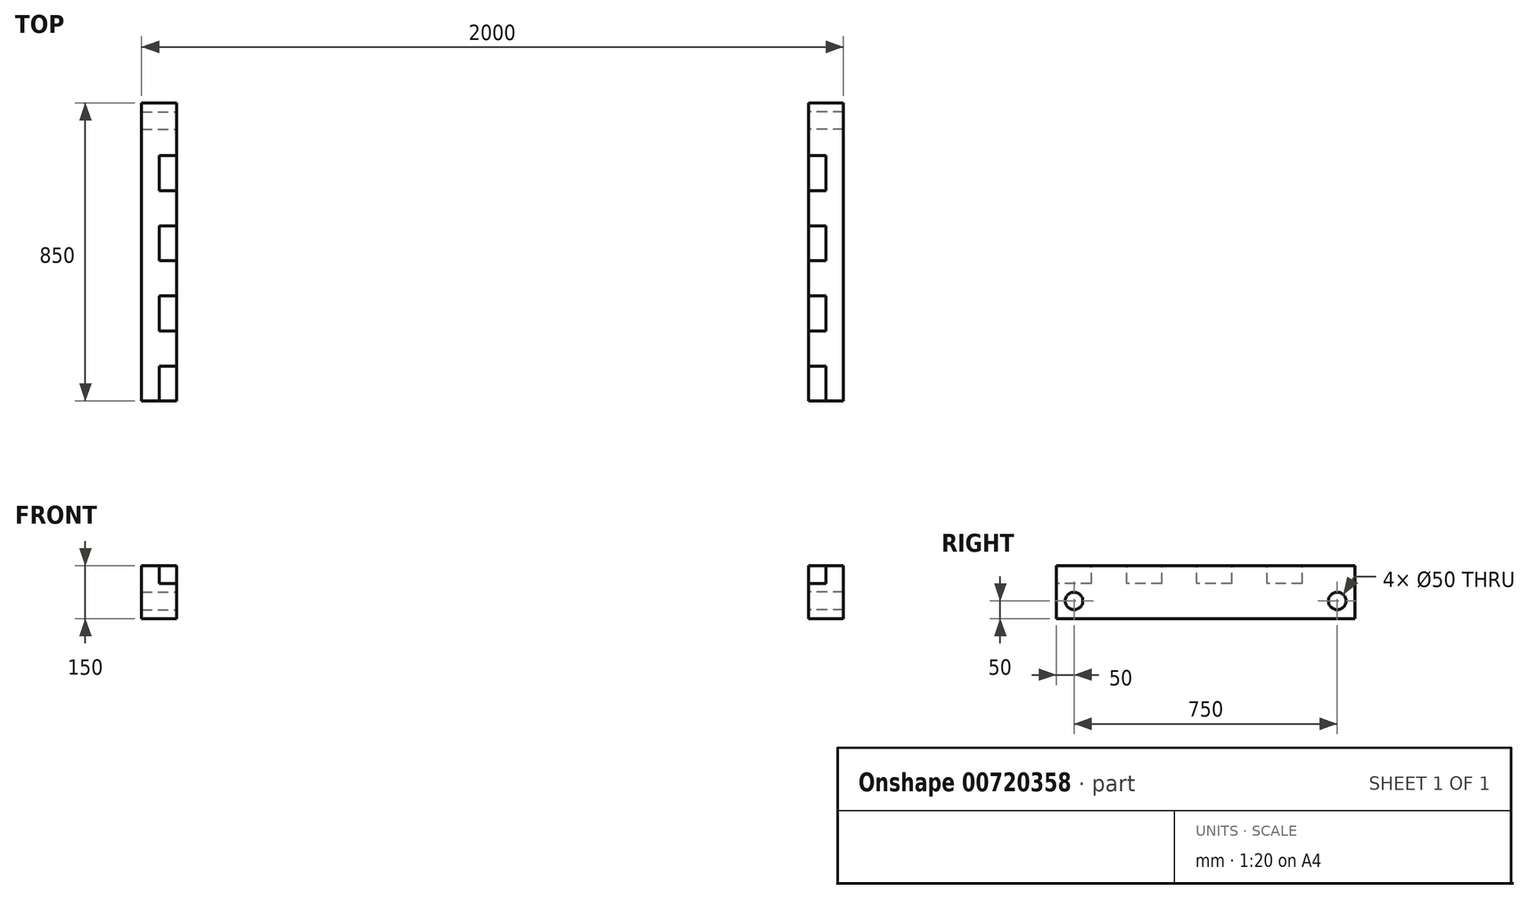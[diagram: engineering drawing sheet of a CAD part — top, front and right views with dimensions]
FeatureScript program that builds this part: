
annotation { "Feature Type Name" : "Feature", "Feature Type Description" : "" }
export const myFeature = defineFeature(function(context is Context, id is Id, definition is map)
    precondition{}
    {
        {
            var Q0;
            Q0=qCreatedBy(makeId("Top.planeOp"),FACE);
            var sketch = newSketch(context, id + "F0", { "sketchPlane" : qUnion([Q0])});
            skLineSegment(sketch, "E0.bottom", {"start": v(1000, 425) * mm, "end": v(-1000, 425) * mm});
            skLineSegment(sketch, "E0.top", {"start": v(1000, -425) * mm, "end": v(-1000, -425) * mm});
            skLineSegment(sketch, "E0.left", {"start": v(1000, 425) * mm, "end": v(1000, -425) * mm});
            skLineSegment(sketch, "E0.right", {"start": v(-1000, 425) * mm, "end": v(-1000, -425) * mm});
            skPoint(sketch, "E0.middle", {"position": v(0, 0) * mm});
            skSolve(sketch);
        }
        {
            var Q0;
            Q0=makeQuery(id+"F0.imprint","IMPRINT",FACE,{"disambiguationData":[TD([[makeQuery(id+"F0.imprint","IMPRINT",EDGE,{"derivedFrom":sQuery(id+"F0.wireOp",EDGE,"E0.bottom")}),1.0]])]});
            extrude(context, id + "F1", {"entities" : qUnion([Q0]), "depth" : 100 * mm, "offsetDistance" : 25 * mm});
        }
        {
            var Q0;
            Q0=makeQuery(id+"F1.opExtrude","CAP_FACE",FACE,{"disambiguationData":[OSD([sQuery(id+"F0.wireOp",EDGE,"E0.bottom"),sQuery(id+"F0.wireOp",EDGE,"E0.top"),sQuery(id+"F0.wireOp",EDGE,"E0.left"),sQuery(id+"F0.wireOp",EDGE,"E0.right")])],"isStart":true});
            var sketch = newSketch(context, id + "F2", { "sketchPlane" : qUnion([Q0])});
            skLineSegment(sketch, "E1.bottom", {"start": v(-900, 425) * mm, "end": v(900, 425) * mm});
            skLineSegment(sketch, "E1.top", {"start": v(-900, -425) * mm, "end": v(900, -425) * mm});
            skLineSegment(sketch, "E1.left", {"start": v(-900, 425) * mm, "end": v(-900, -425) * mm});
            skLineSegment(sketch, "E1.right", {"start": v(900, 425) * mm, "end": v(900, -425) * mm});
            skSolve(sketch);
        }
        {
            var Q0;
            {var subQ0=sQuery(id+"F2.wireOp",EDGE,"E1.left");Q0=makeQuery(id+"F2.imprint","IMPRINT",FACE,{"disambiguationData":[TD([[makeQuery(id+"F2.imprint","IMPRINT",EDGE,{"derivedFrom":subQ0}),-1.0]])]});}
            var Q1;
            {var subQ0=sQuery(id+"F2.wireOp",EDGE,"E1.right");Q1=makeQuery(id+"F2.imprint","IMPRINT",FACE,{"disambiguationData":[TD([[makeQuery(id+"F2.imprint","IMPRINT",EDGE,{"derivedFrom":subQ0}),1.0]])]});}
            extrude(context, id + "F3", {"entities" : qUnion([Q0, Q1]), "operationType" : NewBodyOperationType.ADD, "depth" : 100 * mm, "offsetDistance" : 25 * mm});
        }
        {
            var Q0;
            Q0=makeQuery(id+"F1.opExtrude","CAP_FACE",FACE,{"disambiguationData":[OSD([sQuery(id+"F0.wireOp",EDGE,"E0.bottom"),sQuery(id+"F0.wireOp",EDGE,"E0.top"),sQuery(id+"F0.wireOp",EDGE,"E0.left"),sQuery(id+"F0.wireOp",EDGE,"E0.right")])],"isStart":false});
            var sketch = newSketch(context, id + "F4", { "sketchPlane" : qUnion([Q0])});
            skLineSegment(sketch, "E2.bottom", {"start": v(-800, 425) * mm, "end": v(800, 425) * mm});
            skLineSegment(sketch, "E2.top", {"start": v(-800, -425) * mm, "end": v(800, -425) * mm});
            skLineSegment(sketch, "E2.left", {"start": v(-800, 425) * mm, "end": v(-800, -425) * mm});
            skLineSegment(sketch, "E2.right", {"start": v(800, 425) * mm, "end": v(800, -425) * mm});
            skSolve(sketch);
        }
        {
            var Q0;
            Q0 = qSketchRegion(id + "F4", true);
            extrude(context, id + "F5", {"entities" : qUnion([Q0]), "operationType" : NewBodyOperationType.REMOVE, "oppositeDirection" : true, "depth" : 120 * mm, "offsetDistance" : 25 * mm});
        }
        {
            var Q0;
            Q0=makeQuery(id+"F3.opExtrude","SWEPT_FACE",FACE,{"disambiguationData":[OSD([sQuery(id+"F2.wireOp",EDGE,"E1.left")])]});
            var sketch = newSketch(context, id + "F6", { "sketchPlane" : qUnion([Q0])});
            skCircle(sketch, "E3", {"center": v(-375, -50) * mm, "radius": 25 * mm});
            skPoint(sketch, "E3.centerSnap0", {"position": v(-425, -50) * mm});
            skCircle(sketch, "E4", {"center": v(375, -50) * mm, "radius": 25 * mm});
            skPoint(sketch, "E4.centerSnap0", {"position": v(425, -50) * mm});
            skSolve(sketch);
        }
        {
            var Q0;
            Q0 = qSketchRegion(id + "F6", true);
            extrude(context, id + "F7", {"entities" : qUnion([Q0]), "operationType" : NewBodyOperationType.REMOVE, "oppositeDirection" : true, "depth" : 150 * mm, "offsetDistance" : 25 * mm});
        }
        {
            var Q0;
            Q0=makeQuery(id+"F3.opExtrude","SWEPT_FACE",FACE,{"disambiguationData":[OSD([sQuery(id+"F2.wireOp",EDGE,"E1.right")])]});
            var sketch = newSketch(context, id + "F8", { "sketchPlane" : qUnion([Q0])});
            skCircle(sketch, "E5", {"center": v(375, -50) * mm, "radius": 25 * mm});
            skPoint(sketch, "E5.centerSnap0", {"position": v(425, -50) * mm});
            skCircle(sketch, "E6", {"center": v(-375, -50) * mm, "radius": 25 * mm});
            skPoint(sketch, "E6.centerSnap0", {"position": v(-425, -50) * mm});
            skSolve(sketch);
        }
        {
            var Q0;
            Q0 = qSketchRegion(id + "F8", true);
            extrude(context, id + "F9", {"entities" : qUnion([Q0]), "operationType" : NewBodyOperationType.REMOVE, "oppositeDirection" : true, "depth" : 100 * mm, "offsetDistance" : 25 * mm});
        }
        {
            var Q0;
            {var subQ0=sQuery(id+"F0.wireOp",EDGE,"E0.top");var subQ1=sQuery(id+"F0.wireOp",EDGE,"E0.right");var subQ2=sQuery(id+"F0.wireOp",EDGE,"E0.bottom");var subQ3=sQuery(id+"F0.wireOp",EDGE,"E0.left");Q0=makeQuery(id+"F5.boolean.opBoolean","SPLIT",FACE,{"disambiguationData":[TD([makeQuery(id+"F1.opExtrude","SWEPT_FACE",FACE,{"disambiguationData":[OSD([subQ1])]})])],"derivedFrom":makeQuery(id+"F1.opExtrude","CAP_FACE",FACE,{"disambiguationData":[OSD([subQ2,subQ0,subQ3,subQ1])],"isStart":false})});}
            extrude(context, id + "F10", {"entities" : qUnion([Q0]), "operationType" : NewBodyOperationType.REMOVE, "oppositeDirection" : true, "depth" : 50 * mm, "offsetDistance" : 25 * mm});
        }
        {
            var Q0;
            {var subQ0=sQuery(id+"F0.wireOp",EDGE,"E0.left");var subQ1=sQuery(id+"F0.wireOp",EDGE,"E0.top");var subQ2=sQuery(id+"F0.wireOp",EDGE,"E0.bottom");var subQ9=sQuery(id+"F0.wireOp",EDGE,"E0.right");Q0=makeQuery(id+"F5.boolean.opBoolean","SPLIT",FACE,{"disambiguationData":[TD([makeQuery(id+"F1.opExtrude","SWEPT_FACE",FACE,{"disambiguationData":[OSD([subQ0])]})])],"derivedFrom":makeQuery(id+"F1.opExtrude","CAP_FACE",FACE,{"disambiguationData":[OSD([subQ2,subQ1,subQ0,subQ9])],"isStart":false})});}
            extrude(context, id + "F11", {"entities" : qUnion([Q0]), "operationType" : NewBodyOperationType.REMOVE, "oppositeDirection" : true, "depth" : 50 * mm, "offsetDistance" : 25 * mm});
        }
        {
            var Q0;
            {var subQ0=sQuery(id+"F0.wireOp",EDGE,"E0.left");var subQ2=sQuery(id+"F0.wireOp",EDGE,"E0.right");var subQ3=sQuery(id+"F0.wireOp",EDGE,"E0.top");var subQ5=makeQuery(id+"F1.opExtrude","CAP_EDGE",EDGE,{"disambiguationData":[OSD([subQ3])],"isStart":true});Q0=makeQuery(id+"F5.boolean.opBoolean","SPLIT",FACE,{"disambiguationData":[TD([makeQuery(id+"F1.opExtrude","SWEPT_FACE",FACE,{"disambiguationData":[OSD([subQ0])]})])],"derivedFrom":makeQuery(id+"F3.boolean.opBoolean","MERGE",FACE,{"derivedFrom":[makeQuery(id+"F1.opExtrude","SWEPT_FACE",FACE,{"disambiguationData":[OSD([subQ3])]}),makeQuery(id+"F3.opExtrude","SWEPT_FACE",FACE,{"disambiguationData":[OSD([subQ3]),TDD([makeQuery(id+"F2.imprint","IMPRINT",EDGE,{"disambiguationData":[TD([[makeQuery(id+"F2.imprint","INTERSECT",VERTEX,{"derivedFrom":[subQ5,makeQuery(id+"F1.opExtrude","CAP_EDGE",EDGE,{"disambiguationData":[OSD([subQ0])],"isStart":true})]}),-1.0]])],"derivedFrom":subQ5})])]}),makeQuery(id+"F3.opExtrude","SWEPT_FACE",FACE,{"disambiguationData":[OSD([subQ3]),TDD([makeQuery(id+"F2.imprint","IMPRINT",EDGE,{"disambiguationData":[TD([[makeQuery(id+"F2.imprint","INTERSECT",VERTEX,{"derivedFrom":[subQ5,makeQuery(id+"F1.opExtrude","CAP_EDGE",EDGE,{"disambiguationData":[OSD([subQ2])],"isStart":true})]}),1.0]])],"derivedFrom":subQ5})])]})]})});}
            var sketch = newSketch(context, id + "F12", { "sketchPlane" : qUnion([Q0])});
            skLineSegment(sketch, "E7", {"start": v(900, 0) * mm, "end": v(900, 50) * mm});
            skSolve(sketch);
        }
        {
            var Q0;
            {var subQ0=sQuery(id+"F12.wireOp",EDGE,"E7");Q0=makeQuery(id+"F12.imprint","IMPRINT",FACE,{"disambiguationData":[TD([[makeQuery(id+"F12.imprint","IMPRINT",EDGE,{"derivedFrom":subQ0}),1.0]])]});}
            extrude(context, id + "F13", {"entities" : qUnion([Q0]), "operationType" : NewBodyOperationType.REMOVE, "oppositeDirection" : true, "depth" : 1107 * mm, "offsetDistance" : 25 * mm});
        }
        {
            var Q0;
            {var subQ1=sQuery(id+"F0.wireOp",EDGE,"E0.right");var subQ2=sQuery(id+"F0.wireOp",EDGE,"E0.left");var subQ3=sQuery(id+"F0.wireOp",EDGE,"E0.top");var subQ5=makeQuery(id+"F1.opExtrude","CAP_EDGE",EDGE,{"disambiguationData":[OSD([subQ3])],"isStart":true});Q0=makeQuery(id+"F5.boolean.opBoolean","SPLIT",FACE,{"disambiguationData":[TD([makeQuery(id+"F1.opExtrude","SWEPT_FACE",FACE,{"disambiguationData":[OSD([subQ1])]})])],"derivedFrom":makeQuery(id+"F3.boolean.opBoolean","MERGE",FACE,{"derivedFrom":[makeQuery(id+"F1.opExtrude","SWEPT_FACE",FACE,{"disambiguationData":[OSD([subQ3])]}),makeQuery(id+"F3.opExtrude","SWEPT_FACE",FACE,{"disambiguationData":[OSD([subQ3]),TDD([makeQuery(id+"F2.imprint","IMPRINT",EDGE,{"disambiguationData":[TD([[makeQuery(id+"F2.imprint","INTERSECT",VERTEX,{"derivedFrom":[subQ5,makeQuery(id+"F1.opExtrude","CAP_EDGE",EDGE,{"disambiguationData":[OSD([subQ2])],"isStart":true})]}),-1.0]])],"derivedFrom":subQ5})])]}),makeQuery(id+"F3.opExtrude","SWEPT_FACE",FACE,{"disambiguationData":[OSD([subQ3]),TDD([makeQuery(id+"F2.imprint","IMPRINT",EDGE,{"disambiguationData":[TD([[makeQuery(id+"F2.imprint","INTERSECT",VERTEX,{"derivedFrom":[subQ5,makeQuery(id+"F1.opExtrude","CAP_EDGE",EDGE,{"disambiguationData":[OSD([subQ1])],"isStart":true})]}),1.0]])],"derivedFrom":subQ5})])]})]})});}
            var sketch = newSketch(context, id + "F14", { "sketchPlane" : qUnion([Q0])});
            skLineSegment(sketch, "E8", {"start": v(-900, 0) * mm, "end": v(-900, 50) * mm});
            skSolve(sketch);
        }
        {
            var Q0;
            {var subQ0=sQuery(id+"F14.wireOp",EDGE,"E8");Q0=makeQuery(id+"F14.imprint","IMPRINT",FACE,{"disambiguationData":[TD([[makeQuery(id+"F14.imprint","IMPRINT",EDGE,{"derivedFrom":subQ0}),-1.0]])]});}
            extrude(context, id + "F15", {"entities" : qUnion([Q0]), "operationType" : NewBodyOperationType.REMOVE, "oppositeDirection" : true, "depth" : 1000 * mm, "offsetDistance" : 25 * mm});
        }
        {
            var Q0;
            Q0=makeQuery(id+"F10.boolean.opBoolean","COPY",FACE,{"derivedFrom":makeQuery(id+"F10.opExtrude","CAP_FACE",FACE,{"disambiguationData":[OSD([sQuery(id+"F0.wireOp",EDGE,"E0.bottom"),sQuery(id+"F0.wireOp",EDGE,"E0.top"),sQuery(id+"F0.wireOp",EDGE,"E0.left"),sQuery(id+"F0.wireOp",EDGE,"E0.right")])],"isStart":false})});
            var sketch = newSketch(context, id + "F16", { "sketchPlane" : qUnion([Q0])});
            skLineSegment(sketch, "E9", {"start": v(-950, -425) * mm, "end": v(-950, 425) * mm});
            skLineSegment(sketch, "E10", {"start": v(-950, 375) * mm, "end": v(-900, 375) * mm});
            skLineSegment(sketch, "E11", {"start": v(-950, 275) * mm, "end": v(-900, 275) * mm});
            skLineSegment(sketch, "E12", {"start": v(-950, 175) * mm, "end": v(-900, 175) * mm});
            skLineSegment(sketch, "E13", {"start": v(-950, 75) * mm, "end": v(-900, 75) * mm});
            skLineSegment(sketch, "E14", {"start": v(-950, -25) * mm, "end": v(-900, -25) * mm});
            skLineSegment(sketch, "E15", {"start": v(-950, -125) * mm, "end": v(-900, -125) * mm});
            skLineSegment(sketch, "E16", {"start": v(-950, -225) * mm, "end": v(-900, -225) * mm});
            skLineSegment(sketch, "E17", {"start": v(-950, -325) * mm, "end": v(-900, -325) * mm});
            skSolve(sketch);
        }
        {
            var Q0;
            {var subQ4=sQuery(id+"F16.wireOp",EDGE,"E17");Q0=makeQuery(id+"F16.imprint","IMPRINT",FACE,{"disambiguationData":[TD([[makeQuery(id+"F16.imprint","IMPRINT",EDGE,{"derivedFrom":subQ4}),-1.0]])]});}
            var Q1;
            {var subQ0=sQuery(id+"F16.wireOp",EDGE,"E15");Q1=makeQuery(id+"F16.imprint","IMPRINT",FACE,{"disambiguationData":[TD([[makeQuery(id+"F16.imprint","IMPRINT",EDGE,{"derivedFrom":subQ0}),-1.0]])]});}
            var Q2;
            {var subQ0=sQuery(id+"F16.wireOp",EDGE,"E13");Q2=makeQuery(id+"F16.imprint","IMPRINT",FACE,{"disambiguationData":[TD([[makeQuery(id+"F16.imprint","IMPRINT",EDGE,{"derivedFrom":subQ0}),-1.0]])]});}
            var Q3;
            {var subQ0=sQuery(id+"F16.wireOp",EDGE,"E11");Q3=makeQuery(id+"F16.imprint","IMPRINT",FACE,{"disambiguationData":[TD([[makeQuery(id+"F16.imprint","IMPRINT",EDGE,{"derivedFrom":subQ0}),-1.0]])]});}
            extrude(context, id + "F17", {"entities" : qUnion([Q0, Q1, Q2, Q3]), "operationType" : NewBodyOperationType.REMOVE, "oppositeDirection" : true, "depth" : 50 * mm, "offsetDistance" : 25 * mm});
        }
        {
            var Q0;
            Q0=makeQuery(id+"F11.boolean.opBoolean","COPY",FACE,{"derivedFrom":makeQuery(id+"F11.opExtrude","CAP_FACE",FACE,{"disambiguationData":[OSD([sQuery(id+"F0.wireOp",EDGE,"E0.bottom"),sQuery(id+"F0.wireOp",EDGE,"E0.top"),sQuery(id+"F0.wireOp",EDGE,"E0.left"),sQuery(id+"F0.wireOp",EDGE,"E0.right")])],"isStart":false})});
            var sketch = newSketch(context, id + "F18", { "sketchPlane" : qUnion([Q0])});
            skLineSegment(sketch, "E18", {"start": v(950, -425) * mm, "end": v(950, 425) * mm});
            skLineSegment(sketch, "E19", {"start": v(950, -325) * mm, "end": v(900, -325) * mm});
            skLineSegment(sketch, "E20", {"start": v(950, -225) * mm, "end": v(900, -225) * mm});
            skLineSegment(sketch, "E21", {"start": v(950, -125) * mm, "end": v(900, -125) * mm});
            skLineSegment(sketch, "E22", {"start": v(950, -25) * mm, "end": v(900, -25) * mm});
            skLineSegment(sketch, "E23", {"start": v(950, 75) * mm, "end": v(900, 75) * mm});
            skLineSegment(sketch, "E24", {"start": v(950, 175) * mm, "end": v(900, 175) * mm});
            skLineSegment(sketch, "E25", {"start": v(950, 275) * mm, "end": v(900, 275) * mm});
            skSolve(sketch);
        }
        {
            var Q0;
            {var subQ4=sQuery(id+"F18.wireOp",EDGE,"E19");Q0=makeQuery(id+"F18.imprint","IMPRINT",FACE,{"disambiguationData":[TD([[makeQuery(id+"F18.imprint","IMPRINT",EDGE,{"derivedFrom":subQ4}),1.0]])]});}
            var Q1;
            {var subQ0=sQuery(id+"F18.wireOp",EDGE,"E20");Q1=makeQuery(id+"F18.imprint","IMPRINT",FACE,{"disambiguationData":[TD([[makeQuery(id+"F18.imprint","IMPRINT",EDGE,{"derivedFrom":subQ0}),-1.0]])]});}
            var Q2;
            {var subQ0=sQuery(id+"F18.wireOp",EDGE,"E22");Q2=makeQuery(id+"F18.imprint","IMPRINT",FACE,{"disambiguationData":[TD([[makeQuery(id+"F18.imprint","IMPRINT",EDGE,{"derivedFrom":subQ0}),-1.0]])]});}
            var Q3;
            {var subQ0=sQuery(id+"F18.wireOp",EDGE,"E24");Q3=makeQuery(id+"F18.imprint","IMPRINT",FACE,{"disambiguationData":[TD([[makeQuery(id+"F18.imprint","IMPRINT",EDGE,{"derivedFrom":subQ0}),-1.0]])]});}
            extrude(context, id + "F19", {"entities" : qUnion([Q0, Q1, Q2, Q3]), "operationType" : NewBodyOperationType.REMOVE, "oppositeDirection" : true, "depth" : 50 * mm, "offsetDistance" : 25 * mm});
        }
    });
